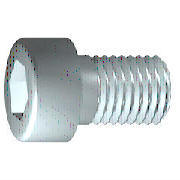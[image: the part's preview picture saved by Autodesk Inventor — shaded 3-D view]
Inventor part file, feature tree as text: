
AUTODESK INVENTOR PART (.ipt)
format: ipt  version: 2022.2 (Build 262287010, 287A)  size: 198,656 bytes
history: native  units: mm (DEFAULTED — no unit token found)
features: sketch x2, extrude x1, plane x1, fillet x1
ambient origin geometry x7: Origin, YZ Plane, XY Plane, X Axis, Y Axis, Z Axis, Center Point
bodies: Solid1 (feature_tree), Body (feature_tree)
feature tree (5):
  extrude  "Slot"  Depth=3.0mm
  plane  "Work Plane1"
  fillet  "Fillet2"  Radius=3.0mm
  sketch  "Sketch1"  dims[d1=8.75mm d2=0.306825mm d3=3.0mm]
  sketch  "Sketch2"  dims[d4=1.3mm d5=60.0deg d6=3.0mm d7=3.0mm d8=2.886751mm d9=5.5mm d10=90.0deg d11=10.0mm d12=0.0mm d13=8.75mm d14=0.0mm d15=0.306725mm d16=0.306725mm d17=0.3mm d19=0.0mm d26=10.0mm d27=45.0deg d28=0.0mm d29=0.0mm d30=0.1mm]
